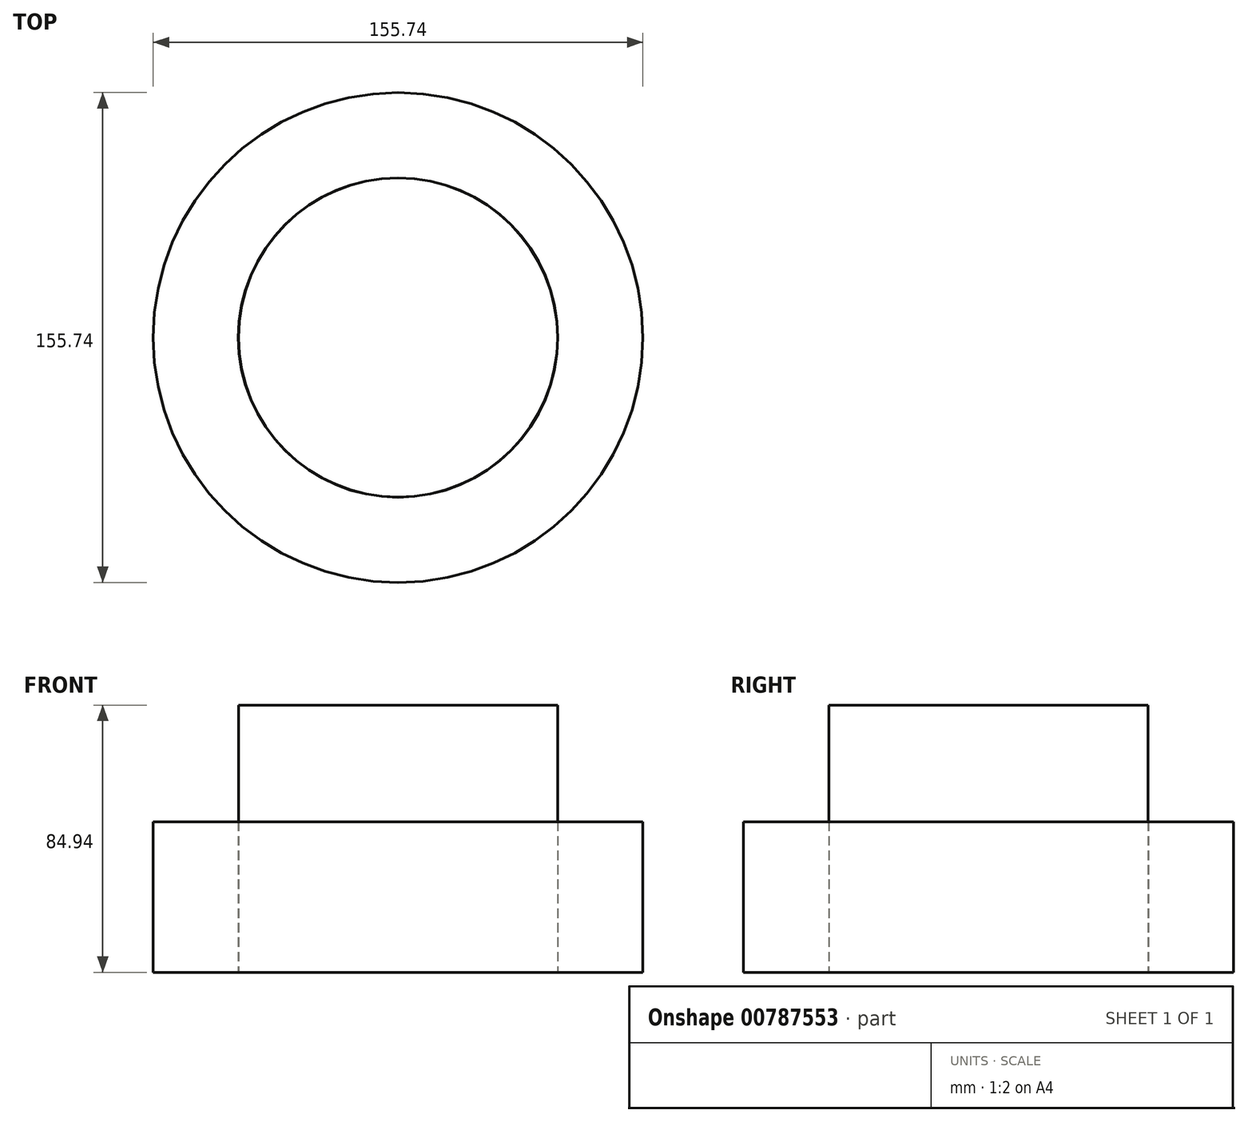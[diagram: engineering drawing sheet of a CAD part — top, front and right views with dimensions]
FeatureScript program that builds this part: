
annotation { "Feature Type Name" : "Feature", "Feature Type Description" : "" }
export const myFeature = defineFeature(function(context is Context, id is Id, definition is map)
    precondition{}
    {
        {
            var Q0;
            Q0=qCreatedBy(makeId("Top.planeOp"),FACE);
            var sketch = newSketch(context, id + "F0", { "sketchPlane" : qUnion([Q0])});
            skCircle(sketch, "E0", {"center": v(0, 0) * mm, "radius": 41.15 * mm});
            skSolve(sketch);
        }
        {
            var Q0;
            Q0=qCreatedBy(makeId("Top.planeOp"),FACE);
            var sketch = newSketch(context, id + "F1", { "sketchPlane" : qUnion([Q0])});
            skCircle(sketch, "E1", {"center": v(0, 0) * mm, "radius": 76.7 * mm});
            skSolve(sketch);
        }
        {
            var Q0;
            Q0=qCreatedBy(makeId("Top.planeOp"),FACE);
            var sketch = newSketch(context, id + "F2", { "sketchPlane" : qUnion([Q0])});
            skCircle(sketch, "E2", {"center": v(0, 0) * mm, "radius": 77.87 * mm});
            skSolve(sketch);
        }
        {
            var Q0;
            Q0=makeQuery(id+"F2.imprint","IMPRINT",FACE,{"disambiguationData":[TD([[makeQuery(id+"F2.imprint","IMPRINT",EDGE,{"derivedFrom":sQuery(id+"F2.wireOp",EDGE,"E2")}),1.0]])]});
            var sketch = newSketch(context, id + "F3", { "sketchPlane" : qUnion([Q0])});
            skSolve(sketch);
        }
        {
            var Q0;
            Q0=makeQuery(id+"F3.imprint","IMPRINT",FACE,{"disambiguationData":[TD([[makeQuery(id+"F3.imprint","IMPRINT",EDGE,{"derivedFrom":makeQuery(id+"F2.imprint","IMPRINT",EDGE,{"derivedFrom":sQuery(id+"F2.wireOp",EDGE,"E2")})}),1.0]])]});
            extrude(context, id + "F4", {"entities" : qUnion([Q0]), "depth" : 47.9 * mm, "offsetDistance" : 25.4 * mm});
        }
        {
            var Q0;
            Q0=sQuery(id+"F1.wireOp",VERTEX,"E1.center");
            var Q1;
            Q1=makeQuery(id+"F4.opExtrude","SWEPT_BODY",BODY,{"disambiguationData":[OSD([sQuery(id+"F2.wireOp",EDGE,"E2")])]});
            hole(context, id + "F5", {"style" : HoleStyle.SIMPLE, "endStyle" : HoleEndStyle.THROUGH, "oppositeDirection" : true, "holeDiameter" : 101.6 * mm, "majorDiameter" : 6.35 * mm, "isTappedThrough" : true, "tappedDepth" : 12.7 * mm, "tapClearance" : 3, "locations" : qUnion([Q0]), "scope" : qUnion([Q1])});
        }
        {
            var Q0;
            Q0=sQuery(id+"F0.wireOp",EDGE,"E0");
            extrude(context, id + "F6", {"bodyType" : ToolBodyType.SURFACE, "surfaceEntities" : qUnion([Q0]), "oppositeDirection" : true, "depth" : 41.66 * mm, "offsetDistance" : 25.4 * mm});
        }
        {
            var Q0;
            Q0=makeQuery(id+"F6.opExtrude","SWEPT_BODY",BODY,{"disambiguationData":[OSD([sQuery(id+"F0.wireOp",EDGE,"E0")])]});
            deleteBodies(context, id + "F7", {"entities" : qUnion([Q0])});
        }
        {
            var Q0;
            Q0 = qSketchRegion(id + "F2", true);
            var sketch = newSketch(context, id + "F8", { "sketchPlane" : qUnion([Q0])});
            skCircle(sketch, "E3", {"center": v(0, 0) * mm, "radius": 50.7 * mm});
            skSolve(sketch);
        }
        {
            var Q0;
            Q0=makeQuery(id+"F8.imprint","IMPRINT",FACE,{"disambiguationData":[TD([[makeQuery(id+"F8.imprint","IMPRINT",EDGE,{"derivedFrom":sQuery(id+"F8.wireOp",EDGE,"E3")}),1.0]])]});
            extrude(context, id + "F9", {"entities" : qUnion([Q0]), "depth" : 84.94 * mm, "offsetDistance" : 25.4 * mm});
        }
    });
